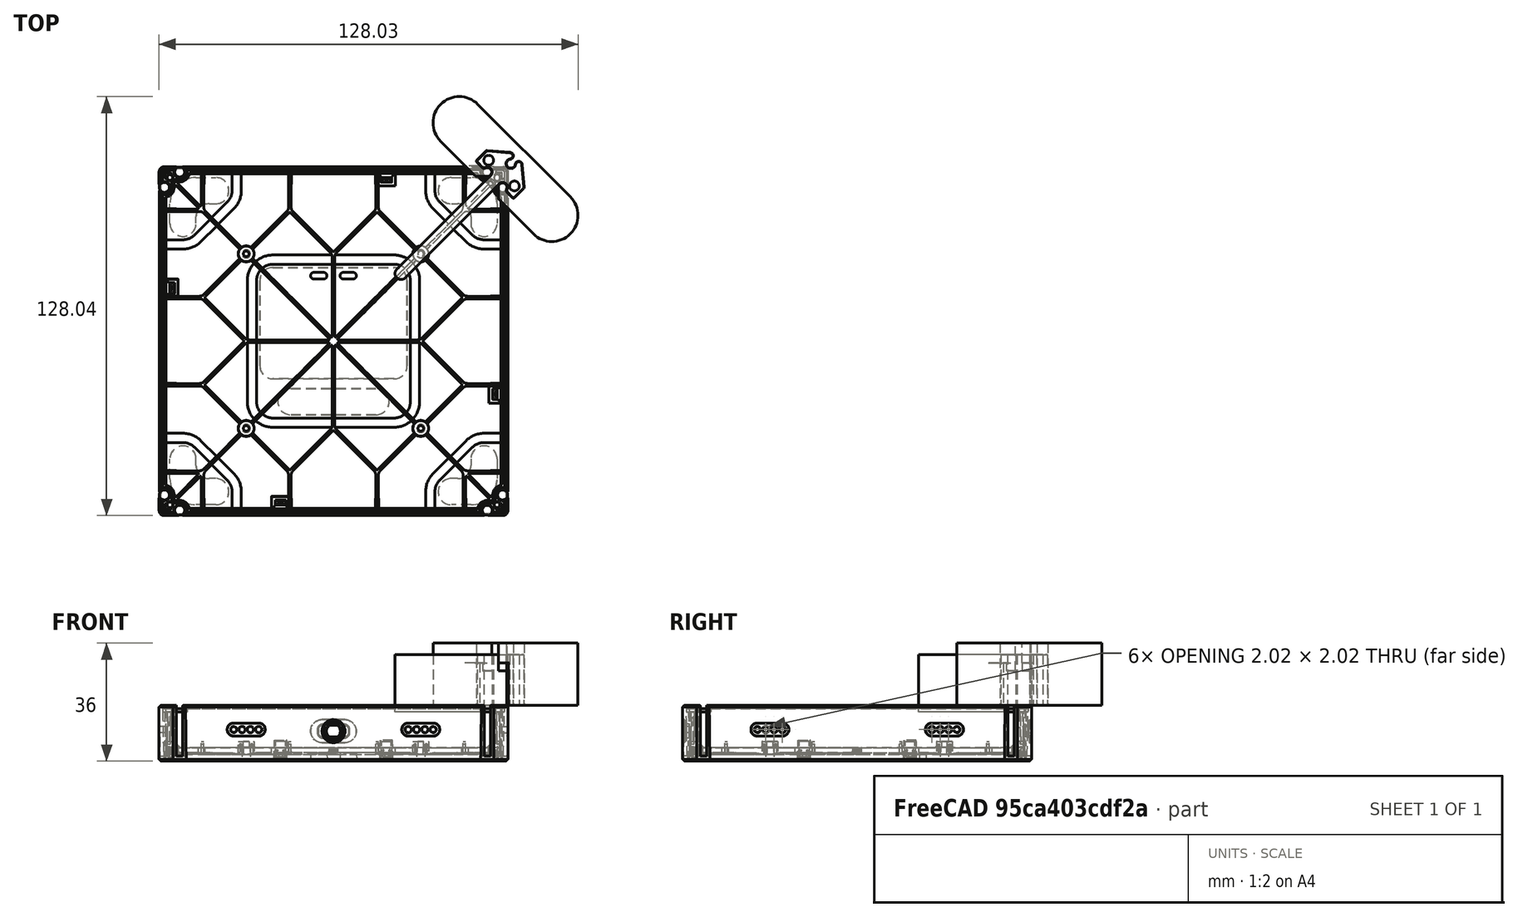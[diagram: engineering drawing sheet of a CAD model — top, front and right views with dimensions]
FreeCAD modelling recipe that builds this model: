
FCSTD DOCUMENT  (FreeCAD 0.21R33771 (Git))
Label: magnet_press_jig_2 part_assy_v2
License: All rights reserved
LicenseURL: https://en.wikipedia.org/wiki/All_rights_reserved
objects: App::FeaturePython×4, Part::FeaturePython×2, Sketcher::SketchObject×1, PartDesign::Body×1
note: 4 computed .brp shape members not serialized (recipe doc carries the construction recipe); baked Part::Feature solids carry a one-line shape summary decoded from their .brp

FEATURE [Part::FeaturePython] b_PLASTIC_CANVAS_001_  label="PLASTIC-CANVAS_001"  # a2plus imported part (geometry in sourceFile) (typed FeaturePython)
  a2p_Version = 0.4.61
  fixedPosition = true
  objectType = a2pPart
  sourceFile = .\..\Mechanical\Design\PLASTIC-CANVAS\PLASTIC-CANVAS.FCStd
  subassemblyImport = false
  timeLastImport = 1.70481e+09
  updateColors = true
FEATURE [Sketcher::SketchObject] Sketch
  FullyConstrained = true
  MapMode = 5
  Support = -> [XY_Plane]
FEATURE [PartDesign::Body] Body
  Group = -> [Sketch]
  Origin = -> Origin
FEATURE [Part::FeaturePython] b_magnet_press_jig_side_2_part_v2_001_  label="magnet_press_jig_side_2 part_v2_001"  # a2plus imported part (geometry in sourceFile) (typed FeaturePython)
  Placement = pos=(51.8768,51.8861,1.50001) rot=(0,0,-1;0.785398rad)
  a2p_Version = 0.4.65
  fixedPosition = false
  objectType = a2pPart
  sourceFile = .\magnet_press_jig_side_2 part_v2.FCStd
  subassemblyImport = false
  timeLastImport = 1.72345e+09
  updateColors = true
FEATURE [App::FeaturePython] planeCoincident_001  label="planeCoincident_001__PLASTIC-CANVAS_001"  # a2plus constraint (typed FeaturePython)
  Object1 = b_magnet_press_jig_side_2_part_v2_001_
  Object2 = b_PLASTIC_CANVAS_001_
  ParentTreeObject = -> b_magnet_press_jig_side_2_part_v2_001_
  SubElement1 = Face1
  SubElement2 = Face371
  Suppressed = false
  Type = plane
  directionConstraint = 0
  offset = 0
FEATURE [App::FeaturePython] planeCoincident_001_mirror  label="planeCoincident_001__magnet_press_jig_side_2 part_v2_001"  # a2plus constraint (typed FeaturePython)
  Object1 = b_magnet_press_jig_side_2_part_v2_001_
  Object2 = b_PLASTIC_CANVAS_001_
  ParentTreeObject = -> b_PLASTIC_CANVAS_001_
  SubElement1 = Face1
  SubElement2 = Face371
  Suppressed = false
  Type = plane
  directionConstraint = 0
  offset = 0
FEATURE [App::FeaturePython] axisCoincident_001  label="axisCoincident_001__PLASTIC-CANVAS_001"  # a2plus constraint (typed FeaturePython)
  Object1 = b_magnet_press_jig_side_2_part_v2_001_
  Object2 = b_PLASTIC_CANVAS_001_
  ParentTreeObject = -> b_magnet_press_jig_side_2_part_v2_001_
  SubElement1 = Edge1
  SubElement2 = Edge1374
  Suppressed = false
  Type = axial
  directionConstraint = 1
  lockRotation = false
FEATURE [App::FeaturePython] axisCoincident_001_mirror  label="axisCoincident_001__magnet_press_jig_side_2 part_v2_001"  # a2plus constraint (typed FeaturePython)
  Object1 = b_magnet_press_jig_side_2_part_v2_001_
  Object2 = b_PLASTIC_CANVAS_001_
  ParentTreeObject = -> b_PLASTIC_CANVAS_001_
  SubElement1 = Edge1
  SubElement2 = Edge1374
  Suppressed = false
  Type = axial
  directionConstraint = 1
  lockRotation = false
